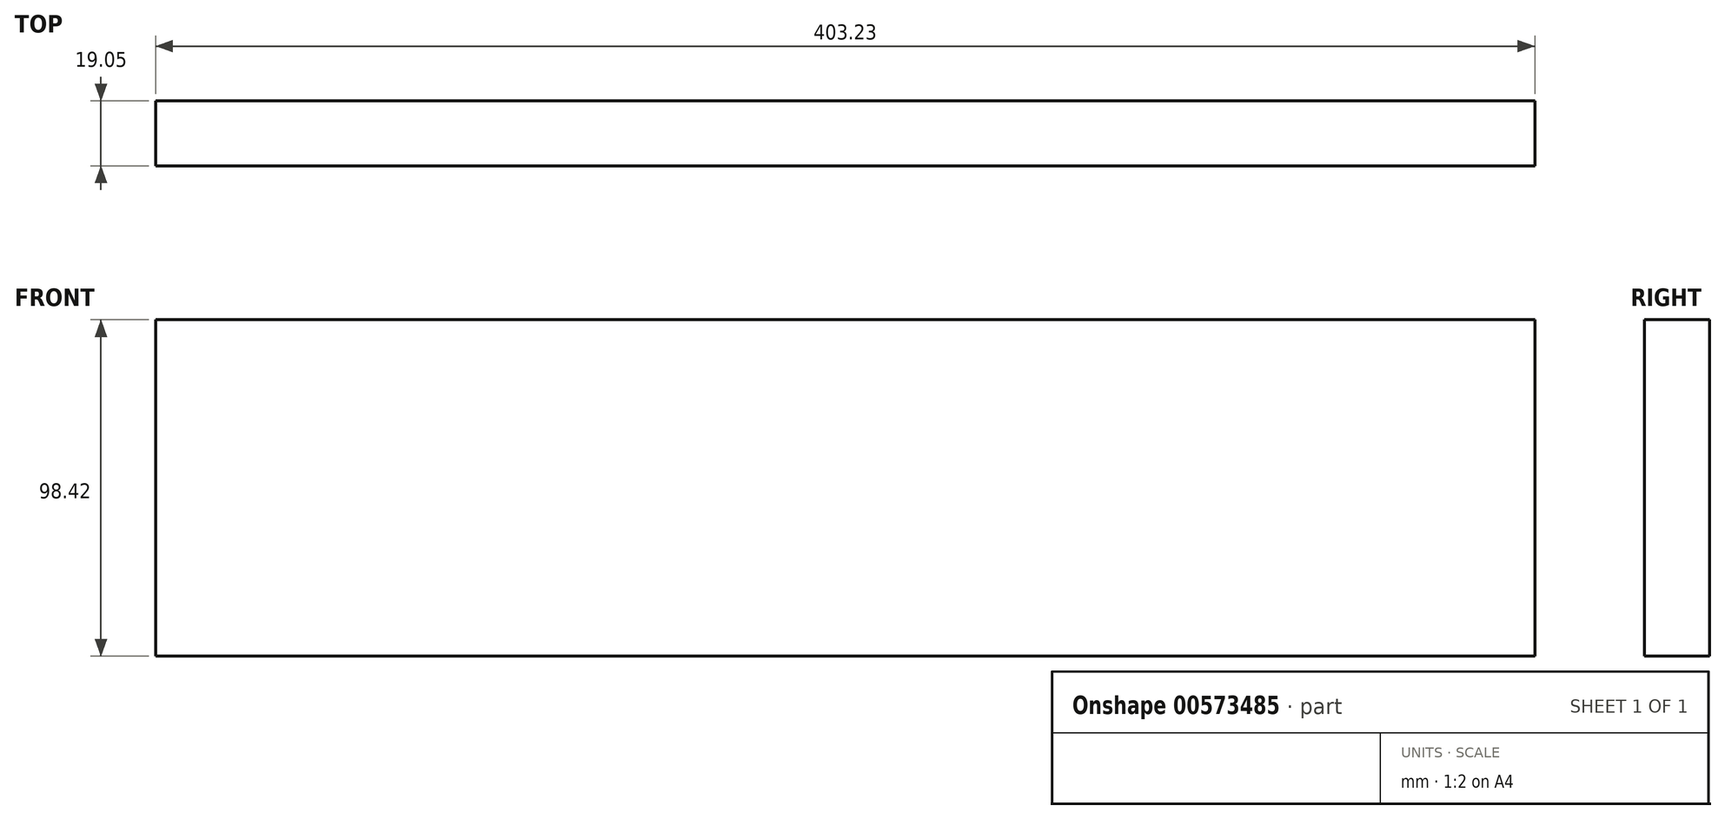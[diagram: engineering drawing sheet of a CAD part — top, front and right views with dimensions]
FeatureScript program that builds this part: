
annotation { "Feature Type Name" : "Feature", "Feature Type Description" : "" }
export const myFeature = defineFeature(function(context is Context, id is Id, definition is map)
    precondition{}
    {
        {
            var Q0;
            Q0=qCreatedBy(makeId("Front.planeOp"),FACE);
            var sketch = newSketch(context, id + "F0", { "sketchPlane" : qUnion([Q0])});
            skLineSegment(sketch, "E0.bottom", {"start": v(0, 0) * mm, "end": v(403.23, 0) * mm});
            skLineSegment(sketch, "E0.top", {"start": v(0, 98.43) * mm, "end": v(403.23, 98.43) * mm});
            skLineSegment(sketch, "E0.left", {"start": v(0, 0) * mm, "end": v(0, 98.43) * mm});
            skLineSegment(sketch, "E0.right", {"start": v(403.23, 0) * mm, "end": v(403.23, 98.43) * mm});
            skSolve(sketch);
        }
        {
            var Q0;
            Q0=makeQuery(id+"F0.imprint","IMPRINT",FACE,{"disambiguationData":[TD([[makeQuery(id+"F0.imprint","IMPRINT",EDGE,{"derivedFrom":sQuery(id+"F0.wireOp",EDGE,"E0.bottom")}),1.0]])]});
            extrude(context, id + "F1", {"entities" : qUnion([Q0]), "depth" : 19.05 * mm, "offsetDistance" : 25.4 * mm});
        }
    });
